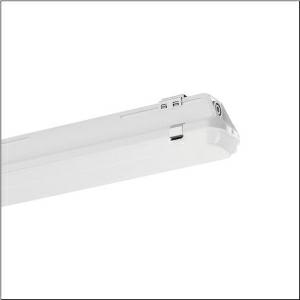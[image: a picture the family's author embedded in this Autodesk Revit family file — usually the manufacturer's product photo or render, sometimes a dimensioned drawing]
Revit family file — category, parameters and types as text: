
# Revit family: monsun_r__21_emergency_51fb107p467b3g_3c42
name_source: partatom
category: Lighting Fixtures
units: mm (PartAtom-declared; Revit-internal decimal feet)

## family parameters
Cut with Voids When Loaded = No
Host = Face
Light Source = No
Part Type = Normal
Room Calculation Point = No
Round Connector Dimension = Use Diameter
Shared = No

## types (1)
- Monsun® 21 emergency (1 x LED, 6060 lm, 42.3 W, 4000K)
    Apparent Load = 42 VA
    CIE Flux Codes = 47 77 93 94 100
    Color Rendering = 80
    Color Temperature = 4000K
    Default Elevation = 1800 mm
    Description = Monsun® 21 emergency, damp-proof luminaire, chain hanger, primary optical cover: enclosure, of PMMA, light emission: direct distribution, primary light characteristic: symmetric, installation type: vertical mounting, horizontal mounting, surface-mounted, suspended mounting, LED, rated luminous flux: 6.060lm, luminous efficacy: 143lm/W, light colour: 840, colour temperature: 4000K, control gear: ECG, with terminal, 4-pole, max. 2.5mm², mains connection: 220..240V, AC, 50/60Hz, rated input power: 42W, control gear: single battery element, battery: NiCd, 4,5Ah, mains connection: 230V, housing, of glass-fibre reinforced polyester, uncoated, bright grey, length: 1.590mm, width: 90mm, height: 88mm, clip for enclosure, of stainless steel (V2A), ceiling mounting element, of stainless steel (V2A), chain hanger, of stainless steel (V2A), protection rating (complete): IP66, insulation class (complete): insulation class I (protective earthing), certification: CE, UKCA, protection symbol: D, impact resistance: IK04, permissible operating ambient temperature: +5..+25°C, standard: EN 60598-2-1, EN 50419, EN 60598-2-22, corresponds to IFS (International Featured Standards) requirements for safety and quality in the food industry, for indoor or canopied outdoor use, no direct snow, no direct sun, no direct rain, packaging unit: 1 piece
    Height = 89 mm
    Lamp = 1 x LED
    Lamp Light Flux = 6060 lm
    Lamp Power = 42.3 W
    Lamp count = 1
    Length = 1590 mm
    Luminous efficacy = 143 lm/W
    Manufacturer = Siteco
    ModVariant = No
    Model = 51FB107P467B3G
    Mounting Place = Ceiling
    Mounting Type = Pendant
    Number of Poles = 1
    OnlyDefault = Yes
    Power Factor = 1
    Product Name = Monsun® 21 emergency
    Product group = damp-proof luminaire | ceiling pendant
    ProductGroupID = 908
    Protection Class = Protection class I
    Protection Degree = IP 66
    RLX_Detail_Level = 1
    RlxData = <blob elided: 88357 chars, md5=a0ca06a3>
    Socket = socket
    Standby Power = 0 W
    System Light Flux = 6060 lm
    System Power = 42 W
    Type Comments = Product without accessories
    Type Image = l_1006717.jpg
    URL = http://relux.com
    VarID = ---
    Voltage = 0 V
    Weight = 0.00 kg
    Width = 90 mm

## geometry (parser evidence)
native form markers: Blend x4, Sweep x14
no freeform markers — native parametric forms only
